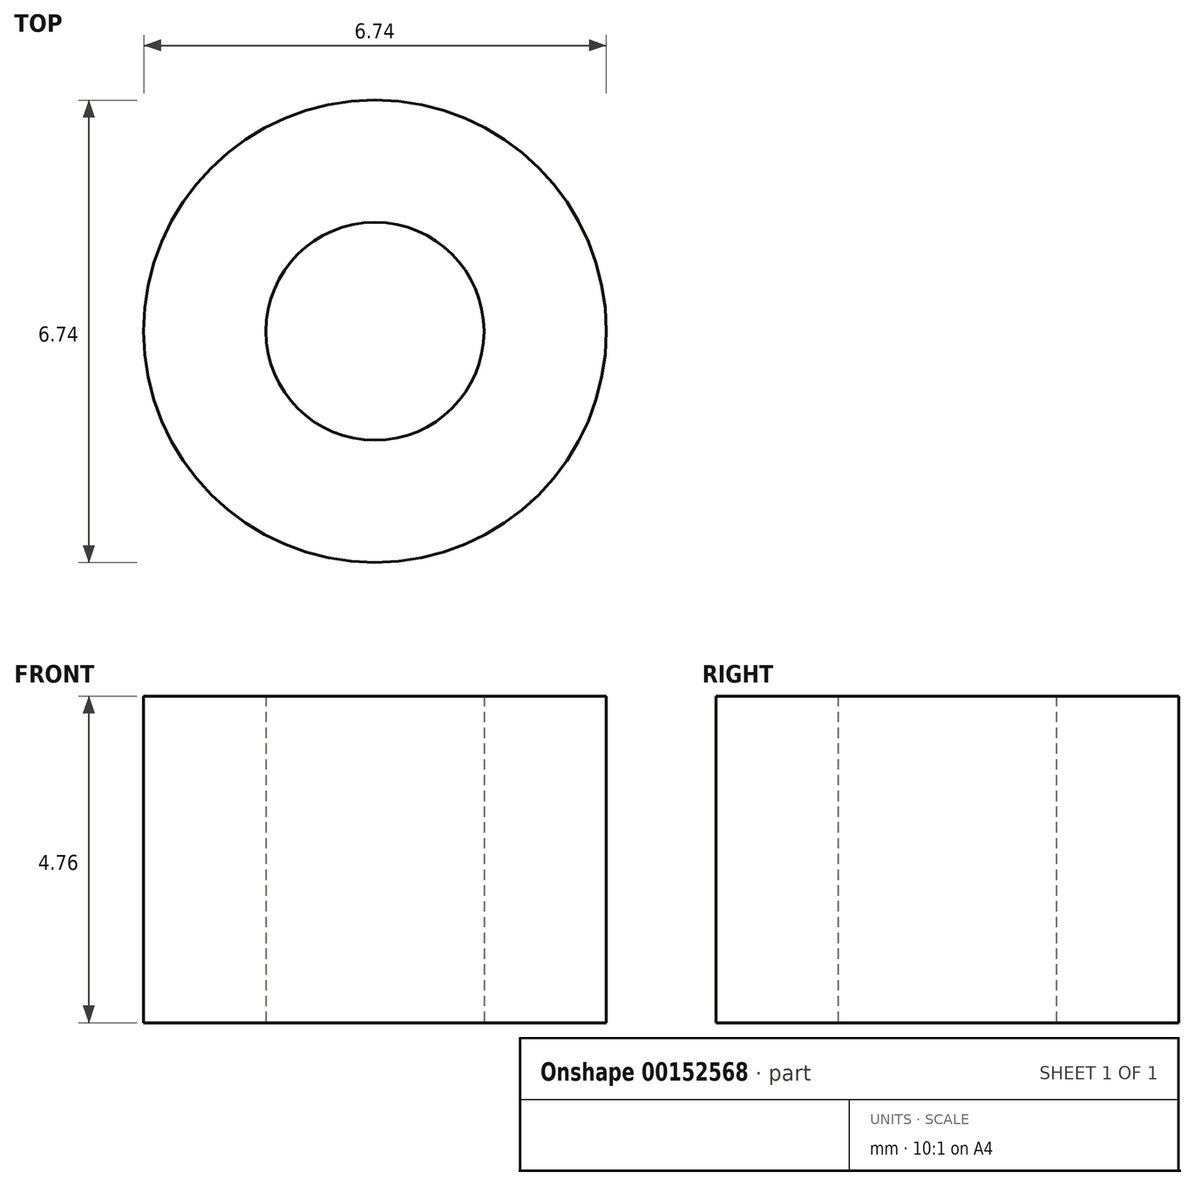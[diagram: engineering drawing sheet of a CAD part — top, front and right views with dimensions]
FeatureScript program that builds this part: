
annotation { "Feature Type Name" : "Feature", "Feature Type Description" : "" }
export const myFeature = defineFeature(function(context is Context, id is Id, definition is map)
    precondition{}
    {
        {
            var Q0;
            Q0=qCreatedBy(makeId("Top.planeOp"),FACE);
            var sketch = newSketch(context, id + "F0", { "sketchPlane" : qUnion([Q0])});
            skCircle(sketch, "E0", {"center": v(0, 0) * mm, "radius": 1.59 * mm});
            skCircle(sketch, "E1", {"center": v(0, 0) * mm, "radius": 3.37 * mm});
            skSolve(sketch);
        }
        {
            var Q0;
            Q0=makeQuery(id+"F0.imprint","IMPRINT",FACE,{"disambiguationData":[TD([[makeQuery(id+"F0.imprint","IMPRINT",EDGE,{"derivedFrom":sQuery(id+"F0.wireOp",EDGE,"E0")}),-1.0]])]});
            extrude(context, id + "F1", {"entities" : qUnion([Q0]), "depth" : 4.76 * mm});
        }
    });
